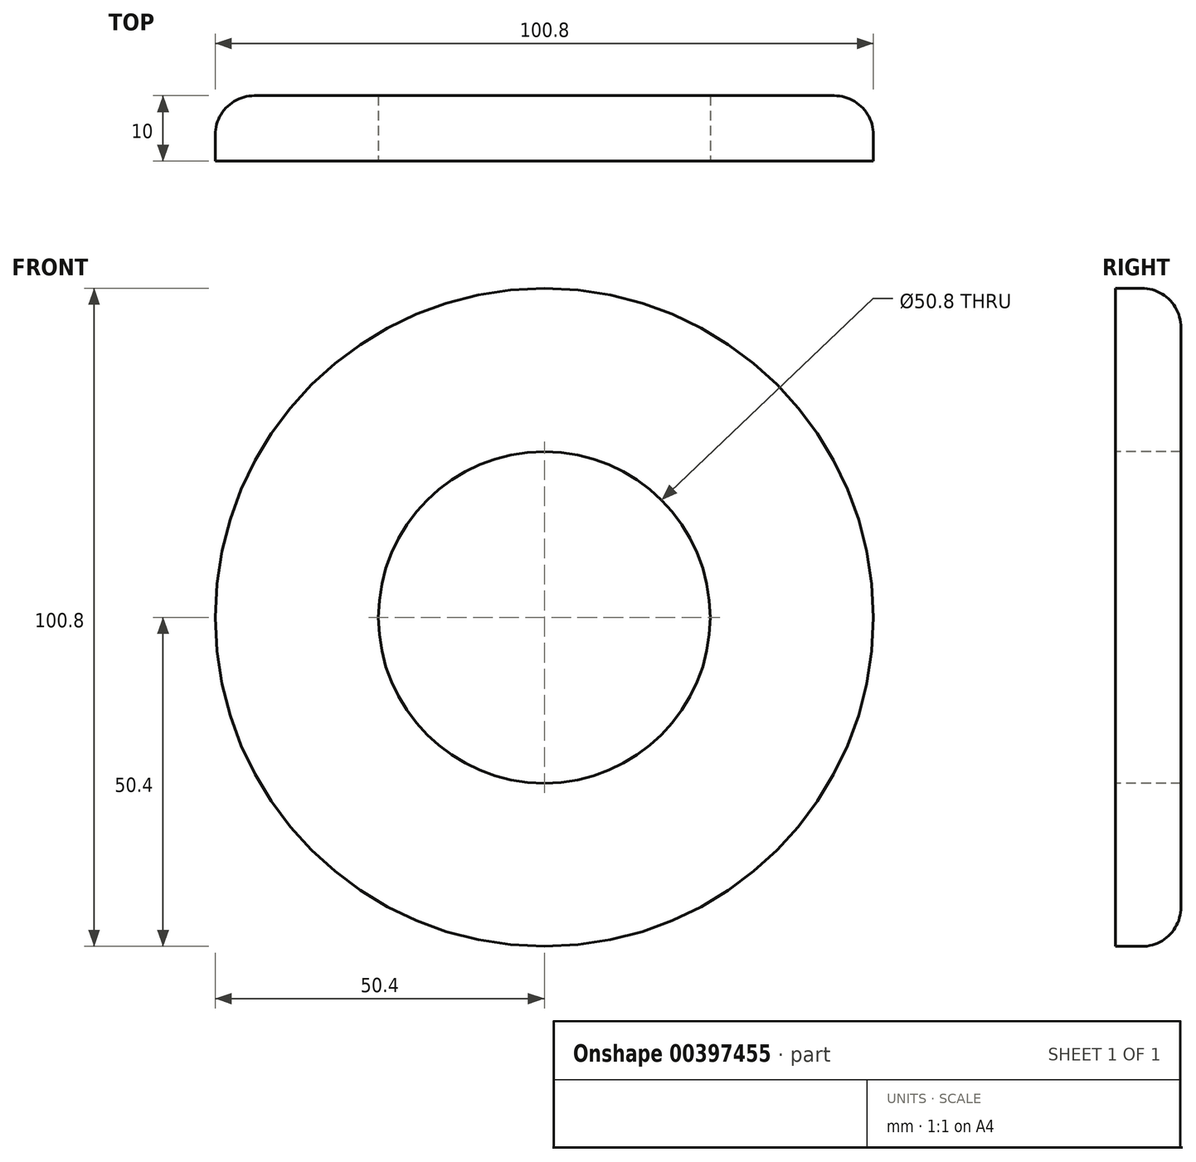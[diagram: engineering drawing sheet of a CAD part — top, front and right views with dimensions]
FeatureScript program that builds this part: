
annotation { "Feature Type Name" : "Feature", "Feature Type Description" : "" }
export const myFeature = defineFeature(function(context is Context, id is Id, definition is map)
    precondition{}
    {
        {
            var Q0;
            Q0=qCreatedBy(makeId("Right.planeOp"),FACE);
            var sketch = newSketch(context, id + "F0", { "sketchPlane" : qUnion([Q0])});
            skLineSegment(sketch, "E0", {"start": v(-25.87, 0) * mm, "end": v(28.96, 0) * mm, "construction": true});
            skLineSegment(sketch, "E1", {"start": v(0, 25.4) * mm, "end": v(10, 25.4) * mm});
            skLineSegment(sketch, "E2", {"start": v(0, 25.4) * mm, "end": v(0, 50.4) * mm});
            skLineSegment(sketch, "E3", {"start": v(0, 50.4) * mm, "end": v(4, 50.4) * mm});
            skLineSegment(sketch, "E4", {"start": v(10, 44.4) * mm, "end": v(10, 25.4) * mm});
            skLineSegment(sketch, "E5.MirrorCS", {"start": v(0, -25.4) * mm, "end": v(10, -25.4) * mm});
            skLineSegment(sketch, "E6.MirrorCS", {"start": v(10, -44.4) * mm, "end": v(10, -25.4) * mm});
            skLineSegment(sketch, "E7.MirrorCS", {"start": v(4, -50.4) * mm, "end": v(10, -44.4) * mm});
            skLineSegment(sketch, "E8.MirrorCS", {"start": v(0, -25.4) * mm, "end": v(0, -50.4) * mm});
            skLineSegment(sketch, "E9.MirrorCS", {"start": v(0, -50.4) * mm, "end": v(4, -50.4) * mm});
            skArc(sketch, "E10", {"start": v(10, 44.4) * mm, "mid": v(8.24, 48.64) * mm, "end": v(4, 50.4) * mm});
            skSolve(sketch);
        }
        {
            var Q0;
            Q0=makeQuery(id+"F0.imprint","IMPRINT",FACE,{"disambiguationData":[TD([[makeQuery(id+"F0.imprint","IMPRINT",EDGE,{"derivedFrom":sQuery(id+"F0.wireOp",EDGE,"E1")}),1.0]])]});
            var Q1;
            Q1=sQuery(id+"F0.wireOp",EDGE,"E0");
            revolve(context, id + "F1", {"entities" : qUnion([Q0]), "axis" : qUnion([Q1]), "revolveType" : RevolveType.FULL});
        }
    });
